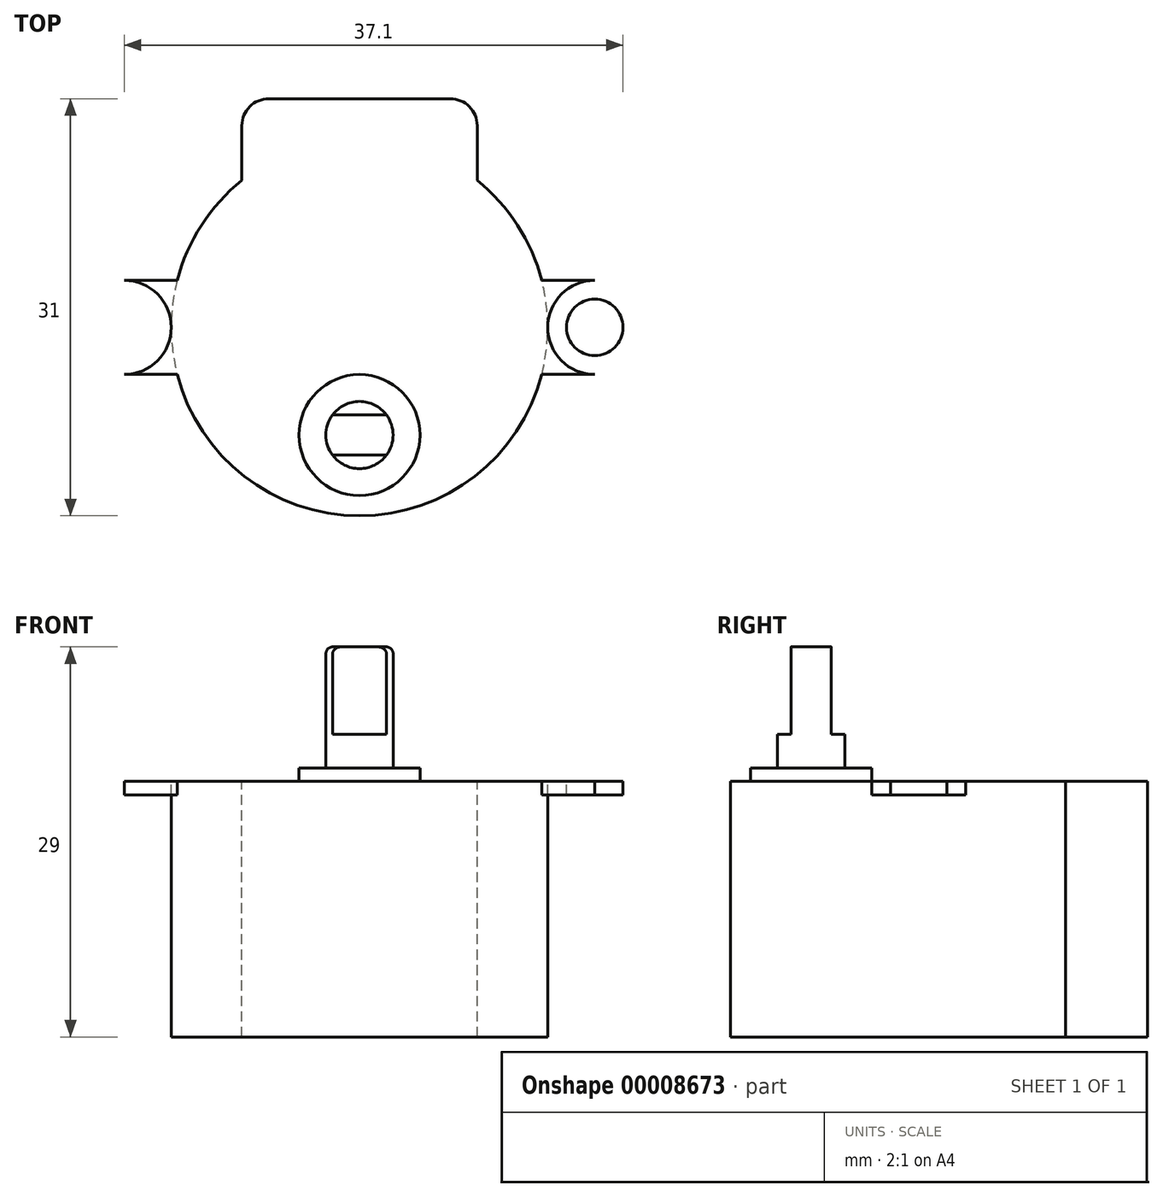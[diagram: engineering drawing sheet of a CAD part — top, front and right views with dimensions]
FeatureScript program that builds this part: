
annotation { "Feature Type Name" : "Feature", "Feature Type Description" : "" }
export const myFeature = defineFeature(function(context is Context, id is Id, definition is map)
    precondition{}
    {
        {
            var Q0;
            Q0=qCreatedBy(makeId("Top.planeOp"),FACE);
            var sketch = newSketch(context, id + "F0", { "sketchPlane" : qUnion([Q0])});
            skCircle(sketch, "E0", {"center": v(0, 0) * mm, "radius": 2.5 * mm});
            skCircle(sketch, "E1", {"center": v(0, 0) * mm, "radius": 4.5 * mm});
            skLineSegment(sketch, "E2.rect.bottom", {"start": v(2, -1.5) * mm, "end": v(-2, -1.5) * mm});
            skLineSegment(sketch, "E2.rect.top", {"start": v(2, 1.5) * mm, "end": v(-2, 1.5) * mm});
            skLineSegment(sketch, "E2.rect.left", {"start": v(2, -1.5) * mm, "end": v(2, 1.5) * mm});
            skLineSegment(sketch, "E2.rect.right", {"start": v(-2, -1.5) * mm, "end": v(-2, 1.5) * mm});
            skCircle(sketch, "E3", {"center": v(0, 8) * mm, "radius": 14 * mm});
            skLineSegment(sketch, "E4", {"start": v(0, 8) * mm, "end": v(0, 0) * mm, "construction": true});
            skLineSegment(sketch, "E5", {"start": v(0, 8) * mm, "end": v(-17.5, 8) * mm, "construction": true});
            skCircle(sketch, "E6", {"center": v(-17.5, 8) * mm, "radius": 3.5 * mm});
            skCircle(sketch, "E7", {"center": v(-17.5, 8) * mm, "radius": 2.1 * mm});
            skLineSegment(sketch, "E8", {"start": v(-17.5, 4.5) * mm, "end": v(-17.5, 11.5) * mm, "construction": true});
            skLineSegment(sketch, "E9", {"start": v(-17.5, 11.5) * mm, "end": v(-13.56, 11.5) * mm});
            skLineSegment(sketch, "E10", {"start": v(-17.5, 4.5) * mm, "end": v(-13.56, 4.5) * mm});
            skLineSegment(sketch, "E11.0.MirrorCS", {"start": v(17.5, 11.5) * mm, "end": v(13.56, 11.5) * mm});
            skLineSegment(sketch, "E11.1.MirrorCS", {"start": v(17.5, 4.5) * mm, "end": v(13.56, 4.5) * mm});
            skCircle(sketch, "E11.2.MirrorC", {"center": v(17.5, 8) * mm, "radius": 2.1 * mm});
            skCircle(sketch, "E11.3.MirrorC", {"center": v(17.5, 8) * mm, "radius": 3.5 * mm});
            skLineSegment(sketch, "E12", {"start": v(0, 8) * mm, "end": v(0, 25) * mm, "construction": true});
            skLineSegment(sketch, "E13.bottom", {"start": v(-6.75, 25) * mm, "end": v(6.75, 25) * mm});
            skLineSegment(sketch, "E13.top", {"start": v(-8.75, 8) * mm, "end": v(8.75, 8) * mm});
            skLineSegment(sketch, "E13.left", {"start": v(-8.75, 23) * mm, "end": v(-8.75, 8) * mm});
            skLineSegment(sketch, "E13.right", {"start": v(8.75, 23) * mm, "end": v(8.75, 8) * mm});
            skPoint(sketch, "E14.visualSharp", {"position": v(-8.75, 25) * mm});
            skArc(sketch, "E14.filletArc", {"start": v(-6.75, 25) * mm, "mid": v(-8.16, 24.41) * mm, "end": v(-8.75, 23) * mm});
            skPoint(sketch, "E15.visualSharp", {"position": v(8.75, 25) * mm});
            skArc(sketch, "E15.filletArc", {"start": v(8.75, 23) * mm, "mid": v(8.16, 24.41) * mm, "end": v(6.75, 25) * mm});
            skSolve(sketch);
        }
        {
            var Q0;
            Q0=makeQuery(id+"F0.imprint","IMPRINT",FACE,{"disambiguationData":[TD([[makeQuery(id+"F0.imprint","IMPRINT",EDGE,{"derivedFrom":sQuery(id+"F0.wireOp",EDGE,"E1")}),1.0]])]});
            extrude(context, id + "F1", {"entities" : qUnion([Q0]), "depth" : 2 * mm, "symmetric" : true});
        }
        {
            var Q0;
            {var subQ0=sQuery(id+"F0.wireOp",EDGE,"E2.rect.top");Q0=makeQuery(id+"F0.imprint","IMPRINT",FACE,{"disambiguationData":[TD([[makeQuery(id+"F0.imprint","IMPRINT",EDGE,{"derivedFrom":subQ0}),-1.0]])]});}
            var Q1;
            Q1=makeQuery(id+"F0.imprint","IMPRINT",FACE,{"disambiguationData":[TD([[makeQuery(id+"F0.imprint","IMPRINT",EDGE,{"derivedFrom":sQuery(id+"F0.wireOp",EDGE,"E2.rect.bottom")}),-1.0]])]});
            var Q2;
            {var subQ0=sQuery(id+"F0.wireOp",EDGE,"E2.rect.bottom");Q2=makeQuery(id+"F0.imprint","IMPRINT",FACE,{"disambiguationData":[TD([[makeQuery(id+"F0.imprint","IMPRINT",EDGE,{"derivedFrom":subQ0}),1.0]])]});}
            var Q3;
            {var subQ0=sQuery(id+"F0.wireOp",EDGE,"E2.rect.left");Q3=makeQuery(id+"F0.imprint","IMPRINT",FACE,{"disambiguationData":[TD([[makeQuery(id+"F0.imprint","IMPRINT",EDGE,{"derivedFrom":subQ0}),-1.0]])]});}
            var Q4;
            {var subQ0=sQuery(id+"F0.wireOp",EDGE,"E2.rect.right");Q4=makeQuery(id+"F0.imprint","IMPRINT",FACE,{"disambiguationData":[TD([[makeQuery(id+"F0.imprint","IMPRINT",EDGE,{"derivedFrom":subQ0}),1.0]])]});}
            extrude(context, id + "F2", {"entities" : qUnion([Q0, Q1, Q2, Q3, Q4]), "depth" : 3.5 * mm});
        }
        {
            var Q0;
            Q0=makeQuery(id+"F0.imprint","IMPRINT",FACE,{"disambiguationData":[TD([[makeQuery(id+"F0.imprint","IMPRINT",EDGE,{"derivedFrom":sQuery(id+"F0.wireOp",EDGE,"E2.rect.bottom")}),-1.0]])]});
            var Q1;
            {var subQ0=sQuery(id+"F0.wireOp",EDGE,"E2.rect.left");Q1=makeQuery(id+"F0.imprint","IMPRINT",FACE,{"disambiguationData":[TD([[makeQuery(id+"F0.imprint","IMPRINT",EDGE,{"derivedFrom":subQ0}),-1.0]])]});}
            var Q2;
            {var subQ0=sQuery(id+"F0.wireOp",EDGE,"E2.rect.right");Q2=makeQuery(id+"F0.imprint","IMPRINT",FACE,{"disambiguationData":[TD([[makeQuery(id+"F0.imprint","IMPRINT",EDGE,{"derivedFrom":subQ0}),1.0]])]});}
            extrude(context, id + "F3", {"entities" : qUnion([Q0, Q1, Q2]), "operationType" : NewBodyOperationType.ADD, "depth" : 10 * mm});
        }
        {
            var Q0;
            {var subQ0=sQuery(id+"F0.wireOp",EDGE,"E0");var subQ1=sQuery(id+"F0.wireOp",EDGE,"E2.rect.left");Q0=makeQuery(id+"F3.opExtrude","CAP_EDGE",EDGE,{"disambiguationData":[OSD([subQ0]),TDD([makeQuery(id+"F0.imprint","IMPRINT",EDGE,{"disambiguationData":[TD([[makeQuery(id+"F0.imprint","INTERSECT",VERTEX,{"derivedFrom":[subQ0,sQuery(id+"F0.wireOp",EDGE,"E2.rect.bottom"),subQ1]}),-1.0]])],"derivedFrom":subQ0})])],"isStart":false});}
            var Q1;
            {var subQ0=sQuery(id+"F0.wireOp",EDGE,"E0");var subQ1=sQuery(id+"F0.wireOp",EDGE,"E2.rect.right");Q1=makeQuery(id+"F3.opExtrude","CAP_EDGE",EDGE,{"disambiguationData":[OSD([subQ0]),TDD([makeQuery(id+"F0.imprint","IMPRINT",EDGE,{"disambiguationData":[TD([[makeQuery(id+"F0.imprint","INTERSECT",VERTEX,{"derivedFrom":[subQ0,sQuery(id+"F0.wireOp",EDGE,"E2.rect.bottom"),subQ1]}),1.0]])],"derivedFrom":subQ0})])],"isStart":false});}
            fillet(context, id + "F4", {"entities" : qUnion([Q0, Q1]), "radius" : .5 * mm, "tangentPropagation" : true, "allowEdgeOverflow" : false});
        }
        {
            var Q0;
            Q0=makeQuery(id+"F0.imprint","IMPRINT",FACE,{"disambiguationData":[TD([[makeQuery(id+"F0.imprint","IMPRINT",EDGE,{"derivedFrom":sQuery(id+"F0.wireOp",EDGE,"E1")}),-1.0]])]});
            var Q1;
            Q1=makeQuery(id+"F0.imprint","IMPRINT",FACE,{"disambiguationData":[TD([[makeQuery(id+"F0.imprint","IMPRINT",EDGE,{"derivedFrom":sQuery(id+"F0.wireOp",EDGE,"E1")}),1.0]])]});
            var Q2;
            {var subQ0=sQuery(id+"F0.wireOp",EDGE,"E2.rect.bottom");Q2=makeQuery(id+"F0.imprint","IMPRINT",FACE,{"disambiguationData":[TD([[makeQuery(id+"F0.imprint","IMPRINT",EDGE,{"derivedFrom":subQ0}),1.0]])]});}
            var Q3;
            {var subQ0=sQuery(id+"F0.wireOp",EDGE,"E2.rect.right");Q3=makeQuery(id+"F0.imprint","IMPRINT",FACE,{"disambiguationData":[TD([[makeQuery(id+"F0.imprint","IMPRINT",EDGE,{"derivedFrom":subQ0}),1.0]])]});}
            var Q4;
            Q4=makeQuery(id+"F0.imprint","IMPRINT",FACE,{"disambiguationData":[TD([[makeQuery(id+"F0.imprint","IMPRINT",EDGE,{"derivedFrom":sQuery(id+"F0.wireOp",EDGE,"E2.rect.bottom")}),-1.0]])]});
            var Q5;
            {var subQ0=sQuery(id+"F0.wireOp",EDGE,"E2.rect.top");Q5=makeQuery(id+"F0.imprint","IMPRINT",FACE,{"disambiguationData":[TD([[makeQuery(id+"F0.imprint","IMPRINT",EDGE,{"derivedFrom":subQ0}),-1.0]])]});}
            var Q6;
            {var subQ0=sQuery(id+"F0.wireOp",EDGE,"E2.rect.left");Q6=makeQuery(id+"F0.imprint","IMPRINT",FACE,{"disambiguationData":[TD([[makeQuery(id+"F0.imprint","IMPRINT",EDGE,{"derivedFrom":subQ0}),-1.0]])]});}
            extrude(context, id + "F5", {"entities" : qUnion([Q0, Q1, Q2, Q3, Q4, Q5, Q6]), "operationType" : NewBodyOperationType.ADD, "oppositeDirection" : true, "depth" : 19 * mm});
        }
        {
            var Q0;
            {var subQ0=sQuery(id+"F0.wireOp",EDGE,"E2.rect.top");Q0=makeQuery(id+"F0.imprint","IMPRINT",FACE,{"disambiguationData":[TD([[makeQuery(id+"F0.imprint","IMPRINT",EDGE,{"derivedFrom":subQ0}),-1.0]])]});}
            var Q1;
            {var subQ0=sQuery(id+"F0.wireOp",EDGE,"E2.rect.left");Q1=makeQuery(id+"F0.imprint","IMPRINT",FACE,{"disambiguationData":[TD([[makeQuery(id+"F0.imprint","IMPRINT",EDGE,{"derivedFrom":subQ0}),-1.0]])]});}
            var Q2;
            {var subQ0=sQuery(id+"F0.wireOp",EDGE,"E2.rect.bottom");Q2=makeQuery(id+"F0.imprint","IMPRINT",FACE,{"disambiguationData":[TD([[makeQuery(id+"F0.imprint","IMPRINT",EDGE,{"derivedFrom":subQ0}),1.0]])]});}
            var Q3;
            {var subQ0=sQuery(id+"F0.wireOp",EDGE,"E2.rect.right");Q3=makeQuery(id+"F0.imprint","IMPRINT",FACE,{"disambiguationData":[TD([[makeQuery(id+"F0.imprint","IMPRINT",EDGE,{"derivedFrom":subQ0}),1.0]])]});}
            var Q4;
            Q4=makeQuery(id+"F0.imprint","IMPRINT",FACE,{"disambiguationData":[TD([[makeQuery(id+"F0.imprint","IMPRINT",EDGE,{"derivedFrom":sQuery(id+"F0.wireOp",EDGE,"E2.rect.bottom")}),-1.0]])]});
            var Q5;
            Q5=makeQuery(id+"F0.imprint","IMPRINT",FACE,{"disambiguationData":[TD([[makeQuery(id+"F0.imprint","IMPRINT",EDGE,{"derivedFrom":sQuery(id+"F0.wireOp",EDGE,"E1")}),1.0]])]});
            var Q6;
            Q6=makeQuery(id+"F0.imprint","IMPRINT",FACE,{"disambiguationData":[TD([[makeQuery(id+"F0.imprint","IMPRINT",EDGE,{"derivedFrom":sQuery(id+"F0.wireOp",EDGE,"E1")}),-1.0]])]});
            var Q7;
            {var subQ3=sQuery(id+"F0.wireOp",EDGE,"E10");Q7=makeQuery(id+"F0.imprint","IMPRINT",FACE,{"disambiguationData":[TD([[makeQuery(id+"F0.imprint","IMPRINT",EDGE,{"derivedFrom":subQ3}),1.0]])]});}
            var Q8;
            {var subQ3=sQuery(id+"F0.wireOp",EDGE,"E9");Q8=makeQuery(id+"F0.imprint","IMPRINT",FACE,{"disambiguationData":[TD([[makeQuery(id+"F0.imprint","IMPRINT",EDGE,{"derivedFrom":subQ3}),-1.0]])]});}
            var Q9;
            Q9=makeQuery(id+"F0.imprint","IMPRINT",FACE,{"disambiguationData":[TD([[makeQuery(id+"F0.imprint","IMPRINT",EDGE,{"derivedFrom":sQuery(id+"F0.wireOp",EDGE,"E7")}),1.0]])]});
            var Q10;
            {var subQ3=sQuery(id+"F0.wireOp",EDGE,"E11.0.MirrorCS");Q10=makeQuery(id+"F0.imprint","IMPRINT",FACE,{"disambiguationData":[TD([[makeQuery(id+"F0.imprint","IMPRINT",EDGE,{"derivedFrom":subQ3}),1.0]])]});}
            var Q11;
            {var subQ3=sQuery(id+"F0.wireOp",EDGE,"E11.1.MirrorCS");Q11=makeQuery(id+"F0.imprint","IMPRINT",FACE,{"disambiguationData":[TD([[makeQuery(id+"F0.imprint","IMPRINT",EDGE,{"derivedFrom":subQ3}),-1.0]])]});}
            var Q12;
            Q12=makeQuery(id+"F0.imprint","IMPRINT",FACE,{"disambiguationData":[TD([[makeQuery(id+"F0.imprint","IMPRINT",EDGE,{"derivedFrom":sQuery(id+"F0.wireOp",EDGE,"E11.2.MirrorC")}),1.0]])]});
            extrude(context, id + "F6", {"entities" : qUnion([Q0, Q1, Q2, Q3, Q4, Q5, Q6, Q7, Q8, Q9, Q10, Q11, Q12]), "operationType" : NewBodyOperationType.ADD, "oppositeDirection" : true, "depth" : 1 * mm});
        }
        {
            var Q0;
            Q0=makeQuery(id+"F0.imprint","IMPRINT",FACE,{"disambiguationData":[TD([[makeQuery(id+"F0.imprint","IMPRINT",EDGE,{"derivedFrom":sQuery(id+"F0.wireOp",EDGE,"E13.bottom")}),-1.0]])]});
            var Q1;
            {var subQ3=sQuery(id+"F0.wireOp",EDGE,"E13.top");Q1=makeQuery(id+"F0.imprint","IMPRINT",FACE,{"disambiguationData":[TD([[makeQuery(id+"F0.imprint","IMPRINT",EDGE,{"derivedFrom":subQ3}),1.0]])]});}
            extrude(context, id + "F7", {"entities" : qUnion([Q0, Q1]), "operationType" : NewBodyOperationType.ADD, "oppositeDirection" : true, "depth" : 19 * mm});
        }
    });
